# Revit family: LXUM
name_source: partatom
category: Mechanical Equipment
units: mm (PartAtom-declared; Revit-internal decimal feet)

## family parameters
Always vertical = Yes
Cut with Voids When Loaded = No
Part Type = Normal
Room Calculation Point = No
Round Connector Dimension = Use Diameter
Shared = No
Work Plane-Based = No

## types (8) — shared parameters
0 = 0' - 0"
1" = 0' - 1"
1' = 1' - 0"
1.5 = 0' - 1 1/2"
2" = 0' - 2"
2' = 2' - 0"
3" = 0' - 3"
4" = 0' - 4"
F = 0' - 0"
Manufacturer = Loren Cook Company
Model = LXUM
ONE EIGTH = 0' - 0 1/8"
Type Comments = Low Silhouette Upblast Exhaust Ventilator Medium Pressure X-Stream Propeller Roof Mounted/Belt Drive
URL = www.lorencook.com

## per-type parameters (varying)
| type | (A/2)-2" | (T_SQ/2)+.125" | -D | -D+2" | -D+4" | A | A/2 | B | B/2 | C | C/2 | D | E | E-.125" | MP/2 | RO/2 | T_SQ | T_SQ/2 | ro |
| 20_LXUM | 0' - 10 1/8" | 1' - 4 1/8" | -1' - 7" | -1' - 5" | -1' - 3" | 2' - 0 1/4" | 1' - 0 1/8" | 2' - 0 1/8" | 1' - 0 1/16" | 1' - 10 1/8" | 0' - 11 1/16" | 1' - 9" | 0' - 2" | 0' - 1 7/8" | 0' - 8" | 1' - 1 3/4" | 2' - 8" | 1' - 4" | 2' - 3 1/2" |
| 24_LXUM | 1' - 1 5/8" | 1' - 6 1/8" | -1' - 6" | -1' - 4" | -1' - 2" | 2' - 7 1/4" | 1' - 3 5/8" | 2' - 4" | 1' - 2" | 2' - 2" | 1' - 1" | 1' - 9" | 0' - 3" | 0' - 2 7/8" | 0' - 9" | 1' - 3 3/4" | 3' - 0" | 1' - 6" | 2' - 7 1/2" |
| 30_LXUM | 1' - 4 5/8" | 1' - 9 1/8" | -1' - 6" | -1' - 4" | -1' - 2" | 3' - 1 1/4" | 1' - 6 5/8" | 2' - 10" | 1' - 5" | 2' - 8" | 1' - 4" | 1' - 9" | 0' - 3" | 0' - 2 7/8" | 0' - 10 1/2" | 1' - 6 3/4" | 3' - 6" | 1' - 9" | 3' - 1 1/2" |
| 36_LXUM | 1' - 7 5/8" | 2' - 0 1/8" | -1' - 6" | -1' - 4" | -1' - 2" | 3' - 7 1/4" | 1' - 9 5/8" | 3' - 2" | 1' - 7" | 3' - 0" | 1' - 6" | 1' - 9" | 0' - 3" | 0' - 2 7/8" | 1' - 0" | 1' - 9 3/4" | 4' - 0" | 2' - 0" | 3' - 7 1/2" |
| 42_LXUM | 1' - 10 5/8" | 2' - 3 1/8" | -1' - 6" | -1' - 4" | -1' - 2" | 4' - 1 1/4" | 2' - 0 5/8" | 3' - 9" | 1' - 10 1/2" | 3' - 7" | 1' - 9 1/2" | 1' - 9" | 0' - 3" | 0' - 2 7/8" | 1' - 1 1/2" | 2' - 0 3/4" | 4' - 6" | 2' - 3" | 4' - 1 1/2" |
| 48_LXUM | 2' - 1 5/8" | 2' - 6 1/8" | -1' - 9" | -1' - 7" | -1' - 5" | 4' - 7 1/4" | 2' - 3 5/8" | 4' - 2" | 2' - 1" | 4' - 0" | 2' - 0" | 2' - 0" | 0' - 3" | 0' - 2 7/8" | 1' - 3" | 2' - 3 3/4" | 5' - 0" | 2' - 6" | 4' - 7 1/2" |
| 54_LXUM | 2' - 4 5/8" | 2' - 9 1/8" | -2' - 1" | -1' - 11" | -1' - 9" | 5' - 1 1/4" | 2' - 6 5/8" | 3' - 10" | 1' - 11" | 3' - 8" | 1' - 10" | 2' - 4" | 0' - 3" | 0' - 2 7/8" | 1' - 4 1/2" | 2' - 6 3/4" | 5' - 6" | 2' - 9" | 5' - 1 1/2" |
| 60_LXUM | 2' - 7 5/8" | 3' - 0 1/8" | -2' - 1" | -1' - 11" | -1' - 9" | 5' - 7 1/4" | 2' - 9 5/8" | 4' - 3" | 2' - 1 1/2" | 4' - 1" | 2' - 0 1/2" | 2' - 4" | 0' - 3" | 0' - 2 7/8" | 1' - 6" | 2' - 9 3/4" | 6' - 0" | 3' - 0" | 5' - 7 1/2" |

## geometry (parser evidence)
native form markers: Sweep x2
no freeform markers — native parametric forms only
